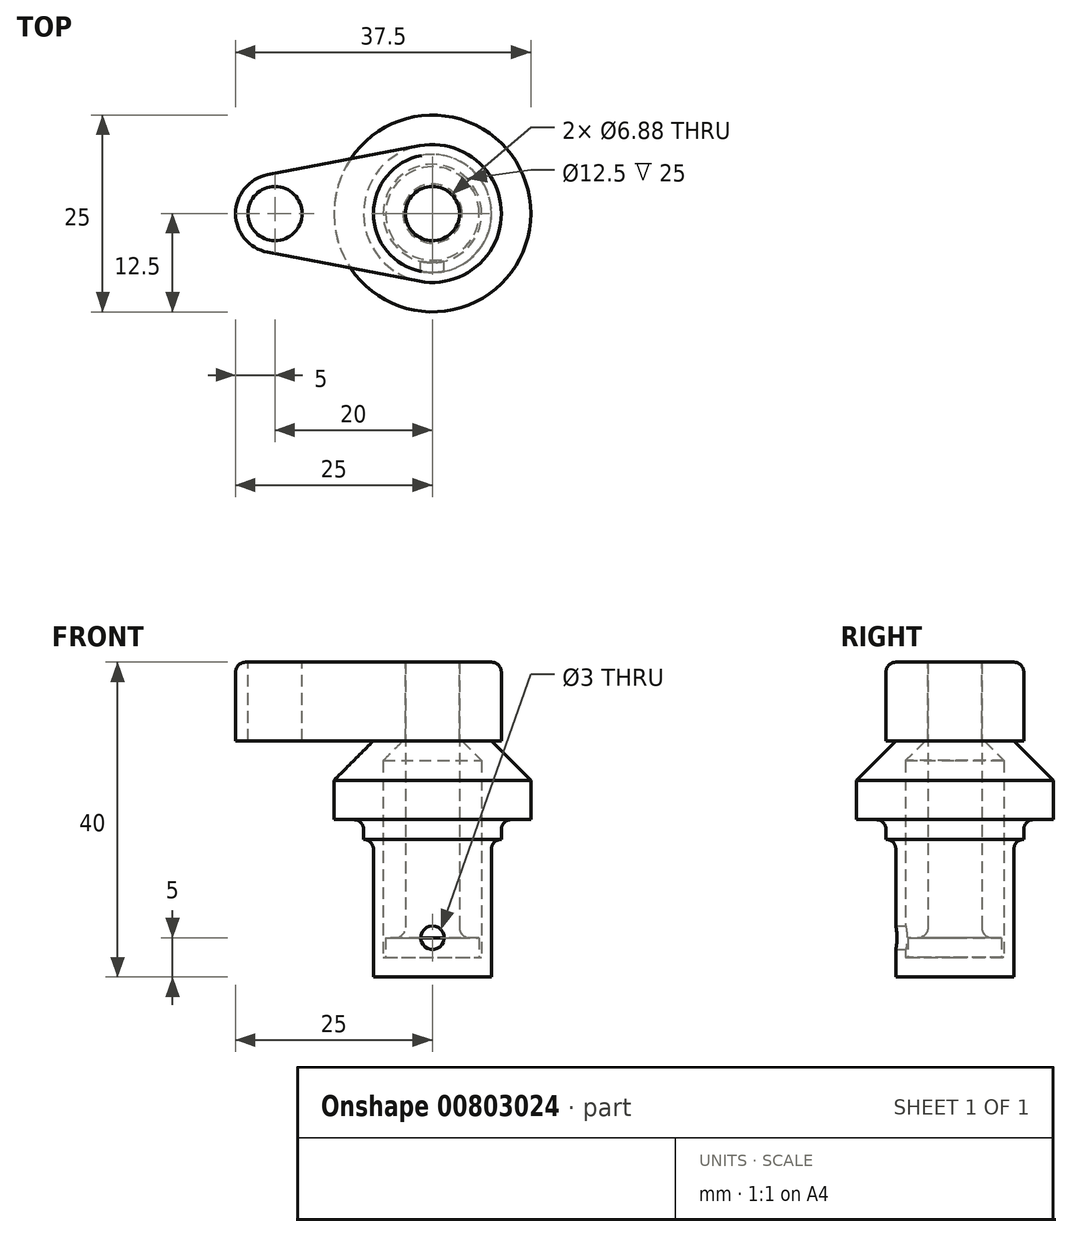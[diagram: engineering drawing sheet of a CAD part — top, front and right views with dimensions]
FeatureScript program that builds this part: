
annotation { "Feature Type Name" : "Feature", "Feature Type Description" : "" }
export const myFeature = defineFeature(function(context is Context, id is Id, definition is map)
    precondition{}
    {
        {
            var Q0;
            Q0=qCreatedBy(makeId("Front.planeOp"),FACE);
            var sketch = newSketch(context, id + "F0", { "sketchPlane" : qUnion([Q0])});
            skLineSegment(sketch, "E0", {"start": v(0, 0) * mm, "end": v(0, 30) * mm});
            skLineSegment(sketch, "E1", {"start": v(0, 30) * mm, "end": v(7.5, 30) * mm});
            skLineSegment(sketch, "E2", {"start": v(7.5, 30) * mm, "end": v(12.5, 25) * mm});
            skLineSegment(sketch, "E3", {"start": v(12.5, 25) * mm, "end": v(12.5, 20) * mm});
            skLineSegment(sketch, "E4", {"start": v(12.5, 20) * mm, "end": v(8.75, 20) * mm});
            skLineSegment(sketch, "E5", {"start": v(8.75, 20) * mm, "end": v(8.75, 17.5) * mm});
            skLineSegment(sketch, "E6", {"start": v(8.75, 17.5) * mm, "end": v(7.5, 17.5) * mm});
            skLineSegment(sketch, "E7", {"start": v(7.5, 17.5) * mm, "end": v(7.5, 0) * mm});
            skLineSegment(sketch, "E8", {"start": v(7.5, 0) * mm, "end": v(0, 0) * mm});
            skLineSegment(sketch, "E9", {"start": v(3.75, 30) * mm, "end": v(6.25, 27.5) * mm});
            skLineSegment(sketch, "E10", {"start": v(6.25, 27.5) * mm, "end": v(6.25, 2.5) * mm});
            skLineSegment(sketch, "E11", {"start": v(6.25, 2.5) * mm, "end": v(0, 2.5) * mm});
            skLineSegment(sketch, "E12", {"start": v(0, 30) * mm, "end": v(0, 41.35) * mm, "construction": true});
            skLineSegment(sketch, "E13", {"start": v(0, 30) * mm, "end": v(0, 40) * mm});
            skLineSegment(sketch, "E14", {"start": v(0, 40) * mm, "end": v(3.44, 40) * mm});
            skLineSegment(sketch, "E15", {"start": v(3.44, 40) * mm, "end": v(3.44, 5) * mm});
            skLineSegment(sketch, "E16", {"start": v(3.44, 5) * mm, "end": v(5.94, 5) * mm});
            skLineSegment(sketch, "E17", {"start": v(5.94, 5) * mm, "end": v(5.94, 2.5) * mm});
            skSolve(sketch);
        }
        {
            var Q0;
            {var subQ4=sQuery(id+"F0.wireOp",EDGE,"E2");Q0=makeQuery(id+"F0.imprint","IMPRINT",FACE,{"disambiguationData":[TD([[makeQuery(id+"F0.imprint","IMPRINT",EDGE,{"derivedFrom":subQ4}),-1.0]])]});}
            var Q1;
            Q1=sQuery(id+"F0.wireOp",EDGE,"E0");
            revolve(context, id + "F1", {"surfaceOperationType" : NewSurfaceOperationType.NEW, "entities" : qUnion([Q0]), "axis" : qUnion([Q1]), "revolveType" : RevolveType.FULL});
        }
        {
            var Q0;
            {var subQ0=sQuery(id+"F0.wireOp",EDGE,"E13");Q0=makeQuery(id+"F0.imprint","IMPRINT",FACE,{"disambiguationData":[TD([[makeQuery(id+"F0.imprint","IMPRINT",EDGE,{"derivedFrom":subQ0}),-1.0]])]});}
            var Q1;
            {var subQ0=sQuery(id+"F0.wireOp",EDGE,"E16");Q1=makeQuery(id+"F0.imprint","IMPRINT",FACE,{"disambiguationData":[TD([[makeQuery(id+"F0.imprint","IMPRINT",EDGE,{"derivedFrom":subQ0}),-1.0]])]});}
            var Q2;
            Q2=sQuery(id+"F0.wireOp",EDGE,"E13");
            revolve(context, id + "F2", {"surfaceOperationType" : NewSurfaceOperationType.NEW, "entities" : qUnion([Q0, Q1]), "axis" : qUnion([Q2]), "revolveType" : RevolveType.FULL});
        }
        {
            var Q0;
            Q0=makeQuery(id+"F2.opRevolve","SWEPT_FACE",FACE,{"disambiguationData":[OSD([sQuery(id+"F0.wireOp",EDGE,"E14")])]});
            var sketch = newSketch(context, id + "F3", { "sketchPlane" : qUnion([Q0])});
            skCircle(sketch, "E18", {"center": v(0, 0) * mm, "radius": 8.75 * mm});
            skCircle(sketch, "E19", {"center": v(-20, 0) * mm, "radius": 5 * mm});
            skLineSegment(sketch, "E20", {"start": v(-1.64, -8.6) * mm, "end": v(-20.94, -4.91) * mm});
            skLineSegment(sketch, "E21", {"start": v(-20.94, 4.91) * mm, "end": v(-1.64, 8.6) * mm});
            skCircle(sketch, "E22.0", {"center": v(0, 0) * mm, "radius": 3.44 * mm});
            skCircle(sketch, "E23", {"center": v(-20, 0) * mm, "radius": 3.44 * mm});
            skSolve(sketch);
        }
        {
            var Q0;
            Q0 = qSketchRegion(id + "F3", true);
            var Q1;
            Q1=makeQuery(id+"F1.opRevolve","SWEPT_FACE",FACE,{"disambiguationData":[OSD([sQuery(id+"F0.wireOp",EDGE,"E1")])]});
            extrude(context, id + "F4", {"entities" : qUnion([Q0]), "endBound" : BoundingType.UP_TO_SURFACE, "oppositeDirection" : true, "depth" : 10 * mm, "endBoundEntityFace" : qUnion([Q1]), "offsetDistance" : 1 * mm});
        }
        {
            var Q0;
            Q0=qCreatedBy(makeId("Front.planeOp"),FACE);
            var sketch = newSketch(context, id + "F5", { "sketchPlane" : qUnion([Q0])});
            skPoint(sketch, "E24", {"position": v(0, 5) * mm});
            skSolve(sketch);
        }
        {
            var Q0;
            Q0=sQuery(id+"F5.wireOp",VERTEX,"E24");
            var Q1;
            Q1=makeQuery(id+"F1.opRevolve","SWEPT_BODY",BODY,{"disambiguationData":[OSD([sQuery(id+"F0.wireOp",EDGE,"E0"),sQuery(id+"F0.wireOp",EDGE,"E1"),sQuery(id+"F0.wireOp",EDGE,"E2"),sQuery(id+"F0.wireOp",EDGE,"E3"),sQuery(id+"F0.wireOp",EDGE,"E4"),sQuery(id+"F0.wireOp",EDGE,"E5"),sQuery(id+"F0.wireOp",EDGE,"E6"),sQuery(id+"F0.wireOp",EDGE,"E7"),sQuery(id+"F0.wireOp",EDGE,"E8"),sQuery(id+"F0.wireOp",EDGE,"E9"),sQuery(id+"F0.wireOp",EDGE,"E10"),sQuery(id+"F0.wireOp",EDGE,"E11")])]});
            hole(context, id + "F6", {"style" : HoleStyle.SIMPLE, "endStyle" : HoleEndStyle.THROUGH, "oppositeDirection" : true, "holeDiameter" : 3 * mm, "majorDiameter" : 5 * mm, "isTappedThrough" : true, "tappedDepth" : 12 * mm, "tapClearance" : 3, "locations" : qUnion([Q0]), "scope" : qUnion([Q1])});
        }
        {
            var Q0;
            Q0=makeQuery(id+"F4.opExtrude","CAP_EDGE",EDGE,{"disambiguationData":[OSD([sQuery(id+"F3.wireOp",EDGE,"E18")])],"isStart":true});
            var Q1;
            Q1=makeQuery(id+"F1.opRevolve","SWEPT_EDGE",EDGE,{"disambiguationData":[OSD([sQuery(id+"F0.wireOp",EDGE,"E4"),sQuery(id+"F0.wireOp",EDGE,"E5")])]});
            var Q2;
            Q2=makeQuery(id+"F1.opRevolve","SWEPT_EDGE",EDGE,{"disambiguationData":[OSD([sQuery(id+"F0.wireOp",EDGE,"E6"),sQuery(id+"F0.wireOp",EDGE,"E7")])]});
            var Q3;
            Q3=makeQuery(id+"F2.opRevolve","SWEPT_EDGE",EDGE,{"disambiguationData":[OSD([sQuery(id+"F0.wireOp",EDGE,"E15"),sQuery(id+"F0.wireOp",EDGE,"E16")])]});
            fillet(context, id + "F7", {"entities" : qUnion([Q0, Q1, Q2, Q3]), "radius" : 1.25 * mm, "tangentPropagation" : true, "allowEdgeOverflow" : false});
        }
    });
